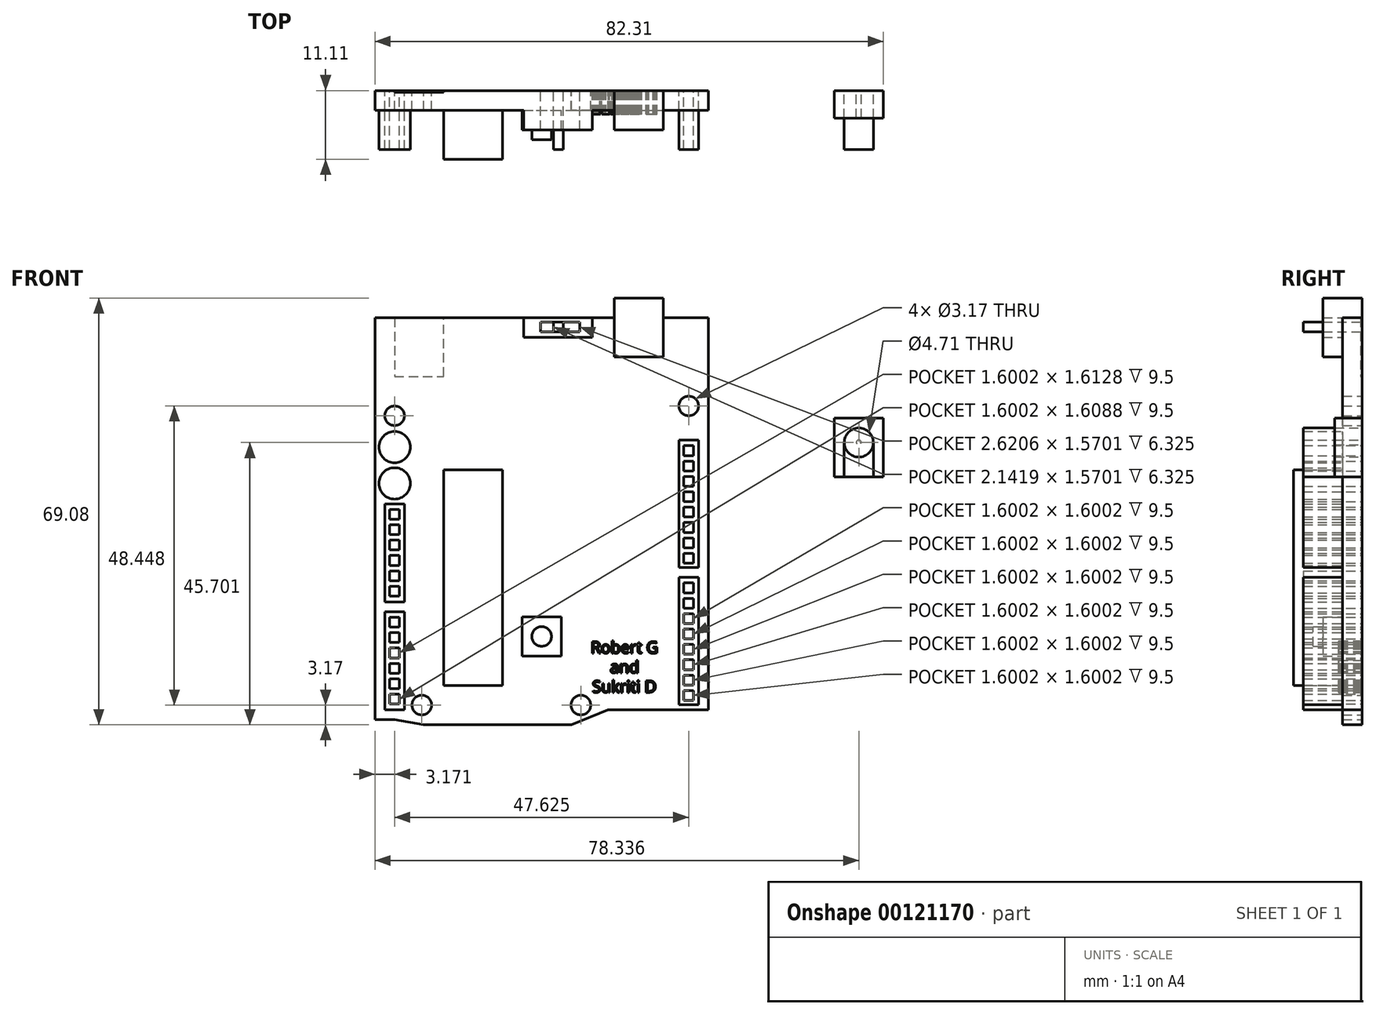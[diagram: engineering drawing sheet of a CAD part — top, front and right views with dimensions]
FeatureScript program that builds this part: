
annotation { "Feature Type Name" : "Feature", "Feature Type Description" : "" }
export const myFeature = defineFeature(function(context is Context, id is Id, definition is map)
    precondition{}
    {
        {
            var Q0;
            Q0=qCreatedBy(makeId("Front.planeOp"),FACE);
            var sketch = newSketch(context, id + "F0", { "sketchPlane" : qUnion([Q0])});
            skLineSegment(sketch, "E0.bottom", {"start": v(-35.3, 35.34) * mm, "end": v(18.68, 35.34) * mm});
            skLineSegment(sketch, "E0.top", {"start": v(-27.43, -30.57) * mm, "end": v(-3.44, -30.57) * mm});
            skLineSegment(sketch, "E0.left", {"start": v(-35.3, 35.34) * mm, "end": v(-35.3, -29.75) * mm});
            skLineSegment(sketch, "E0.right", {"start": v(18.68, 35.34) * mm, "end": v(18.68, -28.16) * mm});
            skLineSegment(sketch, "E1.bottom", {"start": v(-35.3, -29.75) * mm, "end": v(-32.12, -29.75) * mm});
            skPoint(sketch, "E2", {"position": v(-3.44, -30.57) * mm});
            skPoint(sketch, "E3.orphan", {"position": v(18.68, -30.57) * mm});
            skLineSegment(sketch, "E4", {"start": v(-32.12, -29.75) * mm, "end": v(-27.43, -30.57) * mm});
            skPoint(sketch, "E1.right.end.orphan", {"position": v(-35.19, -30.57) * mm});
            skLineSegment(sketch, "E5", {"start": v(-3.44, -30.57) * mm, "end": v(0.98, -28.76) * mm});
            skLineSegment(sketch, "E6", {"start": v(2.42, -28.16) * mm, "end": v(18.68, -28.16) * mm});
            skPoint(sketch, "E7.orphan", {"position": v(18.68, -30.95) * mm});
            skLineSegment(sketch, "E8", {"start": v(0.98, -28.76) * mm, "end": v(2.42, -28.16) * mm});
            skCircle(sketch, "E9", {"center": v(-27.72, -27.39) * mm, "radius": 1.59 * mm});
            skCircle(sketch, "E10", {"center": v(-1.96, -27.4) * mm, "radius": 1.59 * mm});
            skCircle(sketch, "E11", {"center": v(-32.12, 19.46) * mm, "radius": 1.59 * mm});
            skCircle(sketch, "E12", {"center": v(15.5, 21.05) * mm, "radius": 1.59 * mm});
            skLineSegment(sketch, "E13.bottom", {"start": v(11.14, 38.51) * mm, "end": v(11.4, 38.51) * mm});
            skLineSegment(sketch, "E13.top", {"start": v(3.47, 28.99) * mm, "end": v(11.4, 28.99) * mm});
            skLineSegment(sketch, "E14.bottom", {"start": v(13.92, -6.73) * mm, "end": v(17.1, -6.73) * mm});
            skLineSegment(sketch, "E14.top", {"start": v(13.92, -27.37) * mm, "end": v(17.1, -27.37) * mm});
            skLineSegment(sketch, "E14.left", {"start": v(13.92, -6.73) * mm, "end": v(13.92, -27.37) * mm});
            skLineSegment(sketch, "E14.right", {"start": v(17.1, -6.73) * mm, "end": v(17.1, -27.37) * mm});
            skLineSegment(sketch, "E15.bottom", {"start": v(13.92, 15.5) * mm, "end": v(17.1, 15.5) * mm});
            skLineSegment(sketch, "E15.top", {"start": v(13.92, -5.14) * mm, "end": v(17.1, -5.14) * mm});
            skLineSegment(sketch, "E15.left", {"start": v(13.92, 15.5) * mm, "end": v(13.92, -5.14) * mm});
            skLineSegment(sketch, "E15.right", {"start": v(17.1, 15.5) * mm, "end": v(17.1, -5.14) * mm});
            skLineSegment(sketch, "E16.bottom", {"start": v(-33.7, -12.29) * mm, "end": v(-30.53, -12.29) * mm});
            skLineSegment(sketch, "E16.top", {"start": v(-33.7, -28.16) * mm, "end": v(-30.53, -28.16) * mm});
            skLineSegment(sketch, "E16.left", {"start": v(-33.7, -12.29) * mm, "end": v(-33.7, -28.16) * mm});
            skLineSegment(sketch, "E16.right", {"start": v(-30.53, -12.29) * mm, "end": v(-30.53, -28.16) * mm});
            skLineSegment(sketch, "E17", {"start": v(-3.44, -30.57) * mm, "end": v(2.42, -28.16) * mm});
            skLineSegment(sketch, "E18.bottom", {"start": v(-33.7, 5.17) * mm, "end": v(-30.53, 5.17) * mm});
            skLineSegment(sketch, "E18.top", {"start": v(-33.7, -10.7) * mm, "end": v(-30.53, -10.7) * mm});
            skLineSegment(sketch, "E18.left", {"start": v(-33.7, 5.17) * mm, "end": v(-33.7, -10.7) * mm});
            skLineSegment(sketch, "E18.right", {"start": v(-30.53, 5.17) * mm, "end": v(-30.53, -10.7) * mm});
            skLineSegment(sketch, "E19.bottom", {"start": v(-24.18, -24.22) * mm, "end": v(-14.66, -24.22) * mm});
            skLineSegment(sketch, "E19.top", {"start": v(-24.18, 10.7) * mm, "end": v(-14.66, 10.7) * mm});
            skLineSegment(sketch, "E19.left", {"start": v(-24.18, -24.22) * mm, "end": v(-24.18, 10.7) * mm});
            skLineSegment(sketch, "E19.right", {"start": v(-14.66, -24.22) * mm, "end": v(-14.66, 10.7) * mm});
            skLineSegment(sketch, "E20.bottom", {"start": v(-11.48, -13.11) * mm, "end": v(-5.13, -13.11) * mm});
            skLineSegment(sketch, "E20.top", {"start": v(-11.48, -19.46) * mm, "end": v(-5.13, -19.46) * mm});
            skLineSegment(sketch, "E20.left", {"start": v(-11.48, -13.11) * mm, "end": v(-11.48, -19.46) * mm});
            skLineSegment(sketch, "E20.right", {"start": v(-5.13, -13.11) * mm, "end": v(-5.13, -19.46) * mm});
            skCircle(sketch, "E21", {"center": v(-8.3, -16.29) * mm, "radius": 1.59 * mm});
            skLineSegment(sketch, "E22.bottom", {"start": v(-11.2, 32.16) * mm, "end": v(-0.08, 32.16) * mm});
            skLineSegment(sketch, "E22.top", {"start": v(-11.2, 35.34) * mm, "end": v(-0.08, 35.34) * mm});
            skLineSegment(sketch, "E22.left", {"start": v(-11.2, 32.16) * mm, "end": v(-11.2, 35.34) * mm});
            skLineSegment(sketch, "E22.right", {"start": v(-0.08, 32.16) * mm, "end": v(-0.08, 35.34) * mm});
            skLineSegment(sketch, "E23.bottom", {"start": v(-8.5, 33.07) * mm, "end": v(-2.16, 33.07) * mm});
            skLineSegment(sketch, "E23.top", {"start": v(-8.5, 34.64) * mm, "end": v(-2.16, 34.64) * mm});
            skLineSegment(sketch, "E23.left", {"start": v(-8.5, 33.07) * mm, "end": v(-8.5, 34.64) * mm});
            skLineSegment(sketch, "E24", {"start": v(-2.16, 34.64) * mm, "end": v(-2.16, 33.07) * mm});
            skLineSegment(sketch, "E25", {"start": v(-4.78, 34.64) * mm, "end": v(-4.78, 33.07) * mm});
            skLineSegment(sketch, "E26", {"start": v(-6.37, 34.64) * mm, "end": v(-6.37, 33.07) * mm});
            skLineSegment(sketch, "E27", {"start": v(11.4, 36.51) * mm, "end": v(11.4, 35.34) * mm});
            skLineSegment(sketch, "E28.trimOffspring", {"start": v(3.47, 35.34) * mm, "end": v(3.47, 28.99) * mm});
            skLineSegment(sketch, "E29.trimOffspring", {"start": v(11.4, 35.34) * mm, "end": v(11.4, 28.99) * mm});
            skPoint(sketch, "E30.orphan", {"position": v(3.47, 38.51) * mm});
            skLineSegment(sketch, "E31", {"start": v(3.47, 35.34) * mm, "end": v(3.47, 36.51) * mm});
            skLineSegment(sketch, "E32", {"start": v(11.14, 38.51) * mm, "end": v(3.73, 38.51) * mm});
            skLineSegment(sketch, "E33", {"start": v(-32.12, 35.34) * mm, "end": v(-32.12, 25.81) * mm});
            skLineSegment(sketch, "E34", {"start": v(-32.12, 25.81) * mm, "end": v(-24.17, 25.81) * mm});
            skLineSegment(sketch, "E35", {"start": v(-24.17, 25.81) * mm, "end": v(-24.17, 35.34) * mm});
            skLineSegment(sketch, "E36.bottom", {"start": v(-32.9, 4.28) * mm, "end": v(-31.32, 4.28) * mm});
            skLineSegment(sketch, "E36.top", {"start": v(-32.9, 2.7) * mm, "end": v(-31.32, 2.7) * mm});
            skLineSegment(sketch, "E36.left", {"start": v(-32.9, 4.28) * mm, "end": v(-32.9, 2.7) * mm});
            skLineSegment(sketch, "E36.right", {"start": v(-31.32, 4.28) * mm, "end": v(-31.32, 2.7) * mm});
            skLineSegment(sketch, "E37.left", {"start": v(-32.9, 1.25) * mm, "end": v(-32.9, 1.22) * mm});
            skLineSegment(sketch, "E37.right", {"start": v(-31.53, 1.25) * mm, "end": v(-31.53, 1.22) * mm});
            skLineSegment(sketch, "E38.bottom", {"start": v(-32.9, 1.8) * mm, "end": v(-31.32, 1.8) * mm});
            skLineSegment(sketch, "E38.top", {"start": v(-32.9, 0.2) * mm, "end": v(-31.32, 0.2) * mm});
            skLineSegment(sketch, "E38.left", {"start": v(-32.9, 1.8) * mm, "end": v(-32.9, 0.2) * mm});
            skLineSegment(sketch, "E38.right", {"start": v(-31.32, 1.8) * mm, "end": v(-31.32, 0.2) * mm});
            skLineSegment(sketch, "E39.bottom", {"start": v(-32.9, -0.68) * mm, "end": v(-31.32, -0.68) * mm});
            skLineSegment(sketch, "E39.top", {"start": v(-32.9, -2.28) * mm, "end": v(-31.32, -2.28) * mm});
            skLineSegment(sketch, "E39.left", {"start": v(-32.9, -0.68) * mm, "end": v(-32.9, -2.28) * mm});
            skLineSegment(sketch, "E39.right", {"start": v(-31.32, -0.68) * mm, "end": v(-31.32, -2.28) * mm});
            skLineSegment(sketch, "E40.bottom", {"start": v(-32.9, -3.17) * mm, "end": v(-31.32, -3.17) * mm});
            skLineSegment(sketch, "E40.top", {"start": v(-32.9, -4.77) * mm, "end": v(-31.32, -4.77) * mm});
            skLineSegment(sketch, "E40.left", {"start": v(-32.9, -3.17) * mm, "end": v(-32.9, -4.77) * mm});
            skLineSegment(sketch, "E40.right", {"start": v(-31.32, -3.17) * mm, "end": v(-31.32, -4.77) * mm});
            skLineSegment(sketch, "E41.bottom", {"start": v(-32.9, -5.66) * mm, "end": v(-31.32, -5.66) * mm});
            skLineSegment(sketch, "E41.top", {"start": v(-32.9, -7.26) * mm, "end": v(-31.32, -7.26) * mm});
            skLineSegment(sketch, "E41.left", {"start": v(-32.9, -5.66) * mm, "end": v(-32.9, -7.26) * mm});
            skLineSegment(sketch, "E41.right", {"start": v(-31.32, -5.66) * mm, "end": v(-31.32, -7.26) * mm});
            skLineSegment(sketch, "E42.bottom", {"start": v(-32.9, -8.15) * mm, "end": v(-31.32, -8.15) * mm});
            skLineSegment(sketch, "E42.top", {"start": v(-32.9, -9.75) * mm, "end": v(-31.32, -9.75) * mm});
            skLineSegment(sketch, "E42.left", {"start": v(-32.9, -8.15) * mm, "end": v(-32.9, -9.75) * mm});
            skLineSegment(sketch, "E42.right", {"start": v(-31.32, -8.15) * mm, "end": v(-31.32, -9.75) * mm});
            skLineSegment(sketch, "E43.bottom", {"start": v(-32.92, -13.18) * mm, "end": v(-31.32, -13.18) * mm});
            skLineSegment(sketch, "E43.top", {"start": v(-32.92, -14.78) * mm, "end": v(-31.32, -14.78) * mm});
            skLineSegment(sketch, "E43.left", {"start": v(-32.92, -13.18) * mm, "end": v(-32.92, -14.78) * mm});
            skLineSegment(sketch, "E43.right", {"start": v(-31.32, -13.18) * mm, "end": v(-31.32, -14.78) * mm});
            skLineSegment(sketch, "E44.bottom", {"start": v(-32.92, -15.67) * mm, "end": v(-31.32, -15.67) * mm});
            skLineSegment(sketch, "E44.top", {"start": v(-32.92, -17.27) * mm, "end": v(-31.32, -17.27) * mm});
            skLineSegment(sketch, "E44.left", {"start": v(-32.92, -15.67) * mm, "end": v(-32.92, -17.27) * mm});
            skLineSegment(sketch, "E44.right", {"start": v(-31.32, -15.67) * mm, "end": v(-31.32, -17.27) * mm});
            skLineSegment(sketch, "E45.bottom", {"start": v(-32.92, -18.16) * mm, "end": v(-31.32, -18.16) * mm});
            skLineSegment(sketch, "E45.top", {"start": v(-32.92, -19.77) * mm, "end": v(-31.32, -19.77) * mm});
            skLineSegment(sketch, "E45.left", {"start": v(-32.92, -18.16) * mm, "end": v(-32.92, -19.77) * mm});
            skLineSegment(sketch, "E45.right", {"start": v(-31.32, -18.16) * mm, "end": v(-31.32, -19.77) * mm});
            skLineSegment(sketch, "E46.bottom", {"start": v(-32.92, -20.66) * mm, "end": v(-31.32, -20.66) * mm});
            skLineSegment(sketch, "E46.top", {"start": v(-32.92, -22.26) * mm, "end": v(-31.32, -22.26) * mm});
            skLineSegment(sketch, "E46.left", {"start": v(-32.92, -20.66) * mm, "end": v(-32.92, -22.26) * mm});
            skLineSegment(sketch, "E46.right", {"start": v(-31.32, -20.66) * mm, "end": v(-31.32, -22.26) * mm});
            skLineSegment(sketch, "E47.bottom", {"start": v(-32.92, -23.15) * mm, "end": v(-31.32, -23.15) * mm});
            skLineSegment(sketch, "E47.top", {"start": v(-32.92, -24.74) * mm, "end": v(-31.32, -24.74) * mm});
            skLineSegment(sketch, "E47.left", {"start": v(-32.92, -23.15) * mm, "end": v(-32.92, -24.74) * mm});
            skLineSegment(sketch, "E47.right", {"start": v(-31.32, -23.15) * mm, "end": v(-31.32, -24.74) * mm});
            skLineSegment(sketch, "E48.bottom", {"start": v(-32.92, -25.62) * mm, "end": v(-31.32, -25.62) * mm});
            skLineSegment(sketch, "E48.top", {"start": v(-32.92, -27.23) * mm, "end": v(-31.32, -27.23) * mm});
            skLineSegment(sketch, "E48.left", {"start": v(-32.92, -25.62) * mm, "end": v(-32.92, -27.23) * mm});
            skLineSegment(sketch, "E48.right", {"start": v(-31.32, -25.62) * mm, "end": v(-31.32, -27.23) * mm});
            skLineSegment(sketch, "E49.bottom", {"start": v(14.7, 14.6) * mm, "end": v(16.3, 14.6) * mm});
            skLineSegment(sketch, "E49.top", {"start": v(14.7, 13) * mm, "end": v(16.3, 13) * mm});
            skLineSegment(sketch, "E49.left", {"start": v(14.7, 14.6) * mm, "end": v(14.7, 13) * mm});
            skLineSegment(sketch, "E49.right", {"start": v(16.3, 14.6) * mm, "end": v(16.3, 13) * mm});
            skLineSegment(sketch, "E50.bottom", {"start": v(14.7, 12.12) * mm, "end": v(16.3, 12.12) * mm});
            skLineSegment(sketch, "E50.top", {"start": v(14.7, 10.52) * mm, "end": v(16.3, 10.52) * mm});
            skLineSegment(sketch, "E50.left", {"start": v(14.7, 12.12) * mm, "end": v(14.7, 10.52) * mm});
            skLineSegment(sketch, "E50.right", {"start": v(16.3, 12.12) * mm, "end": v(16.3, 10.52) * mm});
            skLineSegment(sketch, "E51.bottom", {"start": v(14.7, 9.63) * mm, "end": v(16.3, 9.63) * mm});
            skLineSegment(sketch, "E51.top", {"start": v(14.7, 8.03) * mm, "end": v(16.3, 8.03) * mm});
            skLineSegment(sketch, "E51.left", {"start": v(14.7, 9.63) * mm, "end": v(14.7, 8.03) * mm});
            skLineSegment(sketch, "E51.right", {"start": v(16.3, 9.63) * mm, "end": v(16.3, 8.03) * mm});
            skLineSegment(sketch, "E52.bottom", {"start": v(14.7, 7.14) * mm, "end": v(16.3, 7.14) * mm});
            skLineSegment(sketch, "E52.top", {"start": v(14.7, 5.54) * mm, "end": v(16.3, 5.54) * mm});
            skLineSegment(sketch, "E52.left", {"start": v(14.7, 7.14) * mm, "end": v(14.7, 5.54) * mm});
            skLineSegment(sketch, "E52.right", {"start": v(16.3, 7.14) * mm, "end": v(16.3, 5.54) * mm});
            skLineSegment(sketch, "E53.bottom", {"start": v(14.7, 4.65) * mm, "end": v(16.3, 4.65) * mm});
            skLineSegment(sketch, "E53.top", {"start": v(14.7, 3.05) * mm, "end": v(16.3, 3.05) * mm});
            skLineSegment(sketch, "E53.left", {"start": v(14.7, 4.65) * mm, "end": v(14.7, 3.05) * mm});
            skLineSegment(sketch, "E53.right", {"start": v(16.3, 4.65) * mm, "end": v(16.3, 3.05) * mm});
            skLineSegment(sketch, "E54.bottom", {"start": v(14.7, 2.16) * mm, "end": v(16.3, 2.16) * mm});
            skLineSegment(sketch, "E54.top", {"start": v(14.7, 0.56) * mm, "end": v(16.3, 0.56) * mm});
            skLineSegment(sketch, "E54.left", {"start": v(14.7, 2.16) * mm, "end": v(14.7, 0.56) * mm});
            skLineSegment(sketch, "E54.right", {"start": v(16.3, 2.16) * mm, "end": v(16.3, 0.56) * mm});
            skLineSegment(sketch, "E55.bottom", {"start": v(14.7, -0.33) * mm, "end": v(16.3, -0.33) * mm});
            skLineSegment(sketch, "E55.top", {"start": v(14.7, -1.92) * mm, "end": v(16.3, -1.92) * mm});
            skLineSegment(sketch, "E55.left", {"start": v(14.7, -0.33) * mm, "end": v(14.7, -1.92) * mm});
            skLineSegment(sketch, "E55.right", {"start": v(16.3, -0.33) * mm, "end": v(16.3, -1.92) * mm});
            skLineSegment(sketch, "E56.bottom", {"start": v(14.7, -2.8) * mm, "end": v(16.3, -2.8) * mm});
            skLineSegment(sketch, "E56.top", {"start": v(14.7, -4.4) * mm, "end": v(16.3, -4.4) * mm});
            skLineSegment(sketch, "E56.left", {"start": v(14.7, -2.8) * mm, "end": v(14.7, -4.4) * mm});
            skLineSegment(sketch, "E56.right", {"start": v(16.3, -2.8) * mm, "end": v(16.3, -4.4) * mm});
            skLineSegment(sketch, "E57.bottom", {"start": v(14.7, -7.62) * mm, "end": v(16.3, -7.62) * mm});
            skLineSegment(sketch, "E57.top", {"start": v(14.7, -9.22) * mm, "end": v(16.3, -9.22) * mm});
            skLineSegment(sketch, "E57.left", {"start": v(14.7, -7.62) * mm, "end": v(14.7, -9.22) * mm});
            skLineSegment(sketch, "E57.right", {"start": v(16.3, -7.62) * mm, "end": v(16.3, -9.22) * mm});
            skLineSegment(sketch, "E58.bottom", {"start": v(14.7, -10.1) * mm, "end": v(16.3, -10.1) * mm});
            skLineSegment(sketch, "E58.top", {"start": v(14.7, -11.7) * mm, "end": v(16.3, -11.7) * mm});
            skLineSegment(sketch, "E58.left", {"start": v(14.7, -10.1) * mm, "end": v(14.7, -11.7) * mm});
            skLineSegment(sketch, "E58.right", {"start": v(16.3, -10.1) * mm, "end": v(16.3, -11.7) * mm});
            skLineSegment(sketch, "E59.bottom", {"start": v(14.7, -12.6) * mm, "end": v(16.3, -12.6) * mm});
            skLineSegment(sketch, "E59.top", {"start": v(14.7, -14.2) * mm, "end": v(16.3, -14.2) * mm});
            skLineSegment(sketch, "E59.left", {"start": v(14.7, -12.6) * mm, "end": v(14.7, -14.2) * mm});
            skLineSegment(sketch, "E59.right", {"start": v(16.3, -12.6) * mm, "end": v(16.3, -14.2) * mm});
            skLineSegment(sketch, "E60.bottom", {"start": v(14.7, -15.09) * mm, "end": v(16.3, -15.09) * mm});
            skLineSegment(sketch, "E60.top", {"start": v(14.7, -16.69) * mm, "end": v(16.3, -16.69) * mm});
            skLineSegment(sketch, "E60.left", {"start": v(14.7, -15.09) * mm, "end": v(14.7, -16.69) * mm});
            skLineSegment(sketch, "E60.right", {"start": v(16.3, -15.09) * mm, "end": v(16.3, -16.69) * mm});
            skLineSegment(sketch, "E61.bottom", {"start": v(14.7, -17.58) * mm, "end": v(16.3, -17.58) * mm});
            skLineSegment(sketch, "E61.top", {"start": v(14.7, -19.18) * mm, "end": v(16.3, -19.18) * mm});
            skLineSegment(sketch, "E61.left", {"start": v(14.7, -17.58) * mm, "end": v(14.7, -19.18) * mm});
            skLineSegment(sketch, "E61.right", {"start": v(16.3, -17.58) * mm, "end": v(16.3, -19.18) * mm});
            skLineSegment(sketch, "E62.bottom", {"start": v(14.7, -20.07) * mm, "end": v(16.3, -20.07) * mm});
            skLineSegment(sketch, "E62.top", {"start": v(14.7, -21.67) * mm, "end": v(16.3, -21.67) * mm});
            skLineSegment(sketch, "E62.left", {"start": v(14.7, -20.07) * mm, "end": v(14.7, -21.67) * mm});
            skLineSegment(sketch, "E62.right", {"start": v(16.3, -20.07) * mm, "end": v(16.3, -21.67) * mm});
            skLineSegment(sketch, "E63.bottom", {"start": v(14.7, -22.56) * mm, "end": v(16.3, -22.56) * mm});
            skLineSegment(sketch, "E63.top", {"start": v(14.7, -24.16) * mm, "end": v(16.3, -24.16) * mm});
            skLineSegment(sketch, "E63.left", {"start": v(14.7, -22.56) * mm, "end": v(14.7, -24.16) * mm});
            skLineSegment(sketch, "E63.right", {"start": v(16.3, -22.56) * mm, "end": v(16.3, -24.16) * mm});
            skLineSegment(sketch, "E64.bottom", {"start": v(14.7, -25.04) * mm, "end": v(16.3, -25.04) * mm});
            skLineSegment(sketch, "E64.top", {"start": v(14.7, -26.64) * mm, "end": v(16.3, -26.64) * mm});
            skLineSegment(sketch, "E64.left", {"start": v(14.7, -25.04) * mm, "end": v(14.7, -26.64) * mm});
            skLineSegment(sketch, "E64.right", {"start": v(16.3, -25.04) * mm, "end": v(16.3, -26.64) * mm});
            skPoint(sketch, "E65.end.orphan", {"position": v(3.73, 37.04) * mm});
            skPoint(sketch, "E66.end.orphan", {"position": v(11.14, 37.04) * mm});
            skLineSegment(sketch, "E67", {"start": v(11.4, 36.51) * mm, "end": v(11.4, 38.51) * mm});
            skLineSegment(sketch, "E68", {"start": v(3.47, 36.51) * mm, "end": v(3.47, 38.51) * mm});
            skLineSegment(sketch, "E69", {"start": v(3.47, 38.51) * mm, "end": v(3.73, 38.51) * mm});
            skCircle(sketch, "E70", {"center": v(-32.12, 8.5) * mm, "radius": 2.54 * mm});
            skCircle(sketch, "E71", {"center": v(-32.12, 14.38) * mm, "radius": 2.54 * mm});
            skPoint(sketch, "E72.left.end.orphan", {"position": v(13.92, 17.84) * mm});
            skPoint(sketch, "E72.bottom.start.orphan", {"position": v(13.92, 16.26) * mm});
            skPoint(sketch, "E72.right.end.orphan", {"position": v(17.1, 17.84) * mm});
            skSolve(sketch);
        }
        {
            var Q0;
            Q0=qCreatedBy(makeId("Front.planeOp"),FACE);
            var sketch = newSketch(context, id + "F1", { "sketchPlane" : qUnion([Q0])});
            skLineSegment(sketch, "E73.bottom", {"start": v(39.08, 19.07) * mm, "end": v(47.02, 19.07) * mm});
            skLineSegment(sketch, "E73.top", {"start": v(39.08, 9.55) * mm, "end": v(47.02, 9.55) * mm});
            skLineSegment(sketch, "E73.left", {"start": v(39.08, 19.07) * mm, "end": v(39.08, 9.55) * mm});
            skLineSegment(sketch, "E73.right", {"start": v(47.02, 19.07) * mm, "end": v(47.02, 9.55) * mm});
            skLineSegment(sketch, "E74", {"start": v(43.05, 12.83) * mm, "end": v(43.05, 12.72) * mm});
            skLineSegment(sketch, "E75", {"start": v(43.05, 12.83) * mm, "end": v(43.05, 12.78) * mm});
            skPoint(sketch, "E76.orphan", {"position": v(43.05, 9.55) * mm});
            skPoint(sketch, "E77", {"position": v(43.05, 17.49) * mm});
            skPoint(sketch, "E78.orphan", {"position": v(43.05, 19.07) * mm});
            skArc(sketch, "E79", {"start": v(43, 12.78) * mm, "mid": v(43.05, 12.78) * mm, "end": v(43.1, 12.78) * mm});
            skCircle(sketch, "E80", {"center": v(43.05, 15.13) * mm, "radius": 0.8 * mm});
            skLineSegment(sketch, "E81", {"start": v(40.7, 15.13) * mm, "end": v(40.7, 9.55) * mm});
            skLineSegment(sketch, "E82", {"start": v(45.4, 15.13) * mm, "end": v(45.4, 9.55) * mm});
            skArc(sketch, "E83.trimOffspring", {"start": v(45.4, 15.13) * mm, "mid": v(43.05, 17.49) * mm, "end": v(40.7, 15.13) * mm});
            skCircle(sketch, "E84", {"center": v(43.05, 15.13) * mm, "radius": 0.4 * mm});
            skArc(sketch, "E85", {"start": v(40.7, 15.13) * mm, "mid": v(43.05, 12.78) * mm, "end": v(45.4, 15.13) * mm});
            skSolve(sketch);
        }
        {
            var Q0;
            {var subQ7=sQuery(id+"F0.wireOp",EDGE,"E0.left");Q0=makeQuery(id+"F0.imprint","IMPRINT",FACE,{"disambiguationData":[TD([[makeQuery(id+"F0.imprint","IMPRINT",EDGE,{"derivedFrom":subQ7}),1.0]])]});}
            var Q1;
            {var subQ0=sQuery(id+"F0.wireOp",EDGE,"E33");Q1=makeQuery(id+"F0.imprint","IMPRINT",FACE,{"disambiguationData":[TD([[makeQuery(id+"F0.imprint","IMPRINT",EDGE,{"derivedFrom":subQ0}),1.0]])]});}
            extrude(context, id + "F2", {"entities" : qUnion([Q0, Q1]), "depth" : 3.17 * mm});
        }
        {
            var Q0;
            Q0=makeQuery(id+"F0.imprint","IMPRINT",FACE,{"disambiguationData":[TD([[makeQuery(id+"F0.imprint","IMPRINT",EDGE,{"derivedFrom":sQuery(id+"F0.wireOp",EDGE,"E22.bottom")}),1.0]])]});
            extrude(context, id + "F3", {"entities" : qUnion([Q0]), "operationType" : NewBodyOperationType.ADD, "depth" : 6.35 * mm});
        }
        {
            var Q0;
            {var subQ0=sQuery(id+"F0.wireOp",EDGE,"E25");Q0=makeQuery(id+"F0.imprint","IMPRINT",FACE,{"disambiguationData":[TD([[makeQuery(id+"F0.imprint","IMPRINT",EDGE,{"derivedFrom":subQ0}),-1.0]])]});}
            extrude(context, id + "F4", {"entities" : qUnion([Q0]), "operationType" : NewBodyOperationType.ADD, "depth" : 9.52 * mm});
        }
        {
            var Q0;
            Q0=makeQuery(id+"F0.imprint","IMPRINT",FACE,{"disambiguationData":[TD([[makeQuery(id+"F0.imprint","IMPRINT",EDGE,{"derivedFrom":sQuery(id+"F0.wireOp",EDGE,"E14.bottom")}),-1.0]])]});
            var Q1;
            Q1=makeQuery(id+"F0.imprint","IMPRINT",FACE,{"disambiguationData":[TD([[makeQuery(id+"F0.imprint","IMPRINT",EDGE,{"derivedFrom":sQuery(id+"F0.wireOp",EDGE,"E15.bottom")}),-1.0]])]});
            var Q2;
            Q2=makeQuery(id+"F0.imprint","IMPRINT",FACE,{"disambiguationData":[TD([[makeQuery(id+"F0.imprint","IMPRINT",EDGE,{"derivedFrom":sQuery(id+"F0.wireOp",EDGE,"E18.bottom")}),-1.0]])]});
            var Q3;
            Q3=makeQuery(id+"F0.imprint","IMPRINT",FACE,{"disambiguationData":[TD([[makeQuery(id+"F0.imprint","IMPRINT",EDGE,{"derivedFrom":sQuery(id+"F0.wireOp",EDGE,"E16.bottom")}),-1.0]])]});
            extrude(context, id + "F5", {"entities" : qUnion([Q0, Q1, Q2, Q3]), "operationType" : NewBodyOperationType.ADD, "depth" : 9.52 * mm});
        }
        {
            var Q0;
            Q0=makeQuery(id+"F0.imprint","IMPRINT",FACE,{"disambiguationData":[TD([[makeQuery(id+"F0.imprint","IMPRINT",EDGE,{"derivedFrom":sQuery(id+"F0.wireOp",EDGE,"E19.bottom")}),1.0]])]});
            extrude(context, id + "F6", {"entities" : qUnion([Q0]), "operationType" : NewBodyOperationType.ADD, "depth" : 11.1 * mm});
        }
        {
            var Q0;
            {var subQ0=sQuery(id+"F0.wireOp",EDGE,"E27");Q0=makeQuery(id+"F0.imprint","IMPRINT",FACE,{"disambiguationData":[TD([[makeQuery(id+"F0.imprint","IMPRINT",EDGE,{"derivedFrom":subQ0}),-1.0]])]});}
            var Q1;
            Q1=makeQuery(id+"F0.imprint","IMPRINT",FACE,{"disambiguationData":[TD([[makeQuery(id+"F0.imprint","IMPRINT",EDGE,{"derivedFrom":sQuery(id+"F0.wireOp",EDGE,"E13.top")}),1.0]])]});
            extrude(context, id + "F7", {"entities" : qUnion([Q0, Q1]), "operationType" : NewBodyOperationType.ADD, "depth" : 6.35 * mm});
        }
        {
            var Q0;
            Q0=makeQuery(id+"F0.imprint","IMPRINT",FACE,{"disambiguationData":[TD([[makeQuery(id+"F0.imprint","IMPRINT",EDGE,{"derivedFrom":sQuery(id+"F0.wireOp",EDGE,"E20.bottom")}),-1.0]])]});
            extrude(context, id + "F8", {"entities" : qUnion([Q0]), "operationType" : NewBodyOperationType.ADD, "depth" : 6.35 * mm});
        }
        {
            var Q0;
            Q0=makeQuery(id+"F0.imprint","IMPRINT",FACE,{"disambiguationData":[TD([[makeQuery(id+"F0.imprint","IMPRINT",EDGE,{"derivedFrom":sQuery(id+"F0.wireOp",EDGE,"E21")}),1.0]])]});
            extrude(context, id + "F9", {"entities" : qUnion([Q0]), "operationType" : NewBodyOperationType.ADD, "depth" : 7.94 * mm});
        }
        {
            var Q0;
            Q0=qCreatedBy(makeId("Front.planeOp"),FACE);
            var sketch = newSketch(context, id + "F10", { "sketchPlane" : qUnion([Q0])});
            skText(sketch, "E86", { "text": "Robert G", "fontName": "OpenSans-Regular.ttf"});
            skText(sketch, "E87", { "text": "and", "fontName": "OpenSans-Regular.ttf"});
            skText(sketch, "E88", { "text": "Sukriti D", "fontName": "OpenSans-Regular.ttf"});
            skLineSegment(sketch, "E89", {"start": v(5.01, -19.27) * mm, "end": v(5.01, -20.54) * mm, "construction": true});
            skLineSegment(sketch, "E90", {"start": v(5.01, -22.45) * mm, "end": v(5.01, -23.72) * mm, "construction": true});
            const initialGuessF10  = {"E86": [-0.00037, -0.019, 1, 0, 0.0019], "E87": [0.00277, -0.02217, 1, 0, 0.0019], "E88": [-0.00012, -0.02534, 1, 0, 0.0019]};
            skSetInitialGuess(sketch, initialGuessF10);
            skSolve(sketch);
        }
        {
            var Q0;
            {var subQ0=sQuery(id+"F0.wireOp",EDGE,"E33");Q0=makeQuery(id+"F0.imprint","IMPRINT",FACE,{"disambiguationData":[TD([[makeQuery(id+"F0.imprint","IMPRINT",EDGE,{"derivedFrom":subQ0}),1.0]])]});}
            extrude(context, id + "F11", {"entities" : qUnion([Q0]), "depth" : 0.25 * mm});
        }
        {
            var Q0;
            Q0=qSketchRegion(id+"F10",true);
            extrude(context, id + "F12", {"entities" : qUnion([Q0]), "depth" : 3.8 * mm});
        }
        {
            var Q0;
            Q0=makeQuery(id+"F1.imprint","IMPRINT",FACE,{"disambiguationData":[TD([[makeQuery(id+"F1.imprint","IMPRINT",EDGE,{"derivedFrom":sQuery(id+"F1.wireOp",EDGE,"E73.bottom")}),-1.0]])]});
            var Q1;
            {var subQ2=sQuery(id+"F1.wireOp",EDGE,"E81");Q1=makeQuery(id+"F1.imprint","IMPRINT",FACE,{"disambiguationData":[TD([[makeQuery(id+"F1.imprint","IMPRINT",EDGE,{"derivedFrom":subQ2}),1.0]])]});}
            var Q2;
            Q2=makeQuery(id+"F1.imprint","IMPRINT",FACE,{"disambiguationData":[TD([[makeQuery(id+"F1.imprint","IMPRINT",EDGE,{"derivedFrom":sQuery(id+"F1.wireOp",EDGE,"E84")}),1.0]])]});
            extrude(context, id + "F13", {"entities" : qUnion([Q0, Q1, Q2]), "depth" : 4.44 * mm});
        }
        {
            var Q0;
            Q0=makeQuery(id+"F1.imprint","IMPRINT",FACE,{"disambiguationData":[TD([[makeQuery(id+"F1.imprint","IMPRINT",EDGE,{"derivedFrom":sQuery(id+"F1.wireOp",EDGE,"E80")}),-1.0]])]});
            var Q1;
            {var subQ2=sQuery(id+"F1.wireOp",EDGE,"E81");Q1=makeQuery(id+"F1.imprint","IMPRINT",FACE,{"disambiguationData":[TD([[makeQuery(id+"F1.imprint","IMPRINT",EDGE,{"derivedFrom":subQ2}),1.0]])]});}
            var Q2;
            Q2=makeQuery(id+"F1.imprint","IMPRINT",FACE,{"disambiguationData":[TD([[makeQuery(id+"F1.imprint","IMPRINT",EDGE,{"derivedFrom":sQuery(id+"F1.wireOp",EDGE,"E80")}),1.0]])]});
            var Q3;
            Q3=makeQuery(id+"F1.imprint","IMPRINT",FACE,{"disambiguationData":[TD([[makeQuery(id+"F1.imprint","IMPRINT",EDGE,{"derivedFrom":sQuery(id+"F1.wireOp",EDGE,"E84")}),1.0]])]});
            extrude(context, id + "F14", {"entities" : qUnion([Q0, Q1, Q2, Q3]), "depth" : 9.52 * mm});
        }
        {
            var Q0;
            Q0=makeQuery(id+"F0.imprint","IMPRINT",FACE,{"disambiguationData":[TD([[makeQuery(id+"F0.imprint","IMPRINT",EDGE,{"derivedFrom":sQuery(id+"F0.wireOp",EDGE,"E39.bottom")}),-1.0]])]});
            var Q1;
            Q1=makeQuery(id+"F0.imprint","IMPRINT",FACE,{"disambiguationData":[TD([[makeQuery(id+"F0.imprint","IMPRINT",EDGE,{"derivedFrom":sQuery(id+"F0.wireOp",EDGE,"E38.bottom")}),-1.0]])]});
            var Q2;
            Q2=makeQuery(id+"F0.imprint","IMPRINT",FACE,{"disambiguationData":[TD([[makeQuery(id+"F0.imprint","IMPRINT",EDGE,{"derivedFrom":sQuery(id+"F0.wireOp",EDGE,"E36.bottom")}),-1.0]])]});
            var Q3;
            Q3=makeQuery(id+"F0.imprint","IMPRINT",FACE,{"disambiguationData":[TD([[makeQuery(id+"F0.imprint","IMPRINT",EDGE,{"derivedFrom":sQuery(id+"F0.wireOp",EDGE,"E40.bottom")}),-1.0]])]});
            var Q4;
            Q4=makeQuery(id+"F0.imprint","IMPRINT",FACE,{"disambiguationData":[TD([[makeQuery(id+"F0.imprint","IMPRINT",EDGE,{"derivedFrom":sQuery(id+"F0.wireOp",EDGE,"E42.bottom")}),-1.0]])]});
            var Q5;
            Q5=makeQuery(id+"F0.imprint","IMPRINT",FACE,{"disambiguationData":[TD([[makeQuery(id+"F0.imprint","IMPRINT",EDGE,{"derivedFrom":sQuery(id+"F0.wireOp",EDGE,"E41.bottom")}),-1.0]])]});
            extrude(context, id + "F15", {"entities" : qUnion([Q0, Q1, Q2, Q3, Q4, Q5]), "operationType" : NewBodyOperationType.ADD, "depth" : 0.03 * mm});
        }
        {
            var Q0;
            Q0=makeQuery(id+"F0.imprint","IMPRINT",FACE,{"disambiguationData":[TD([[makeQuery(id+"F0.imprint","IMPRINT",EDGE,{"derivedFrom":sQuery(id+"F0.wireOp",EDGE,"E43.bottom")}),-1.0]])]});
            var Q1;
            Q1=makeQuery(id+"F0.imprint","IMPRINT",FACE,{"disambiguationData":[TD([[makeQuery(id+"F0.imprint","IMPRINT",EDGE,{"derivedFrom":sQuery(id+"F0.wireOp",EDGE,"E44.bottom")}),-1.0]])]});
            var Q2;
            Q2=makeQuery(id+"F0.imprint","IMPRINT",FACE,{"disambiguationData":[TD([[makeQuery(id+"F0.imprint","IMPRINT",EDGE,{"derivedFrom":sQuery(id+"F0.wireOp",EDGE,"E45.bottom")}),-1.0]])]});
            var Q3;
            Q3=makeQuery(id+"F0.imprint","IMPRINT",FACE,{"disambiguationData":[TD([[makeQuery(id+"F0.imprint","IMPRINT",EDGE,{"derivedFrom":sQuery(id+"F0.wireOp",EDGE,"E46.bottom")}),-1.0]])]});
            var Q4;
            Q4=makeQuery(id+"F0.imprint","IMPRINT",FACE,{"disambiguationData":[TD([[makeQuery(id+"F0.imprint","IMPRINT",EDGE,{"derivedFrom":sQuery(id+"F0.wireOp",EDGE,"E47.bottom")}),-1.0]])]});
            var Q5;
            Q5=makeQuery(id+"F0.imprint","IMPRINT",FACE,{"disambiguationData":[TD([[makeQuery(id+"F0.imprint","IMPRINT",EDGE,{"derivedFrom":sQuery(id+"F0.wireOp",EDGE,"E48.bottom")}),-1.0]])]});
            extrude(context, id + "F16", {"entities" : qUnion([Q0, Q1, Q2, Q3, Q4, Q5]), "operationType" : NewBodyOperationType.ADD, "depth" : 0.03 * mm});
        }
        {
            var Q0;
            Q0=makeQuery(id+"F0.imprint","IMPRINT",FACE,{"disambiguationData":[TD([[makeQuery(id+"F0.imprint","IMPRINT",EDGE,{"derivedFrom":sQuery(id+"F0.wireOp",EDGE,"E49.bottom")}),-1.0]])]});
            var Q1;
            Q1=makeQuery(id+"F0.imprint","IMPRINT",FACE,{"disambiguationData":[TD([[makeQuery(id+"F0.imprint","IMPRINT",EDGE,{"derivedFrom":sQuery(id+"F0.wireOp",EDGE,"E55.bottom")}),-1.0]])]});
            var Q2;
            Q2=makeQuery(id+"F0.imprint","IMPRINT",FACE,{"disambiguationData":[TD([[makeQuery(id+"F0.imprint","IMPRINT",EDGE,{"derivedFrom":sQuery(id+"F0.wireOp",EDGE,"E54.bottom")}),-1.0]])]});
            var Q3;
            Q3=makeQuery(id+"F0.imprint","IMPRINT",FACE,{"disambiguationData":[TD([[makeQuery(id+"F0.imprint","IMPRINT",EDGE,{"derivedFrom":sQuery(id+"F0.wireOp",EDGE,"E53.bottom")}),-1.0]])]});
            var Q4;
            Q4=makeQuery(id+"F0.imprint","IMPRINT",FACE,{"disambiguationData":[TD([[makeQuery(id+"F0.imprint","IMPRINT",EDGE,{"derivedFrom":sQuery(id+"F0.wireOp",EDGE,"E52.bottom")}),-1.0]])]});
            var Q5;
            Q5=makeQuery(id+"F0.imprint","IMPRINT",FACE,{"disambiguationData":[TD([[makeQuery(id+"F0.imprint","IMPRINT",EDGE,{"derivedFrom":sQuery(id+"F0.wireOp",EDGE,"E51.bottom")}),-1.0]])]});
            var Q6;
            Q6=makeQuery(id+"F0.imprint","IMPRINT",FACE,{"disambiguationData":[TD([[makeQuery(id+"F0.imprint","IMPRINT",EDGE,{"derivedFrom":sQuery(id+"F0.wireOp",EDGE,"E50.bottom")}),-1.0]])]});
            var Q7;
            Q7=makeQuery(id+"F0.imprint","IMPRINT",FACE,{"disambiguationData":[TD([[makeQuery(id+"F0.imprint","IMPRINT",EDGE,{"derivedFrom":sQuery(id+"F0.wireOp",EDGE,"E56.bottom")}),-1.0]])]});
            extrude(context, id + "F17", {"entities" : qUnion([Q0, Q1, Q2, Q3, Q4, Q5, Q6, Q7]), "operationType" : NewBodyOperationType.ADD, "depth" : 0.03 * mm});
        }
        {
            var Q0;
            {var subQ0=sQuery(id+"F0.wireOp",EDGE,"E24");Q0=makeQuery(id+"F0.imprint","IMPRINT",FACE,{"disambiguationData":[TD([[makeQuery(id+"F0.imprint","IMPRINT",EDGE,{"derivedFrom":subQ0}),-1.0]])]});}
            var Q1;
            {var subQ0=sQuery(id+"F0.wireOp",EDGE,"E23.left");Q1=makeQuery(id+"F0.imprint","IMPRINT",FACE,{"disambiguationData":[TD([[makeQuery(id+"F0.imprint","IMPRINT",EDGE,{"derivedFrom":subQ0}),-1.0]])]});}
            extrude(context, id + "F18", {"entities" : qUnion([Q0, Q1]), "operationType" : NewBodyOperationType.ADD, "depth" : 0.03 * mm});
        }
        {
            var Q0;
            Q0=makeQuery(id+"F0.imprint","IMPRINT",FACE,{"disambiguationData":[TD([[makeQuery(id+"F0.imprint","IMPRINT",EDGE,{"derivedFrom":sQuery(id+"F0.wireOp",EDGE,"E59.bottom")}),-1.0]])]});
            var Q1;
            Q1=makeQuery(id+"F0.imprint","IMPRINT",FACE,{"disambiguationData":[TD([[makeQuery(id+"F0.imprint","IMPRINT",EDGE,{"derivedFrom":sQuery(id+"F0.wireOp",EDGE,"E61.bottom")}),-1.0]])]});
            var Q2;
            Q2=makeQuery(id+"F0.imprint","IMPRINT",FACE,{"disambiguationData":[TD([[makeQuery(id+"F0.imprint","IMPRINT",EDGE,{"derivedFrom":sQuery(id+"F0.wireOp",EDGE,"E60.bottom")}),-1.0]])]});
            var Q3;
            Q3=makeQuery(id+"F0.imprint","IMPRINT",FACE,{"disambiguationData":[TD([[makeQuery(id+"F0.imprint","IMPRINT",EDGE,{"derivedFrom":sQuery(id+"F0.wireOp",EDGE,"E62.bottom")}),-1.0]])]});
            var Q4;
            Q4=makeQuery(id+"F0.imprint","IMPRINT",FACE,{"disambiguationData":[TD([[makeQuery(id+"F0.imprint","IMPRINT",EDGE,{"derivedFrom":sQuery(id+"F0.wireOp",EDGE,"E63.bottom")}),-1.0]])]});
            var Q5;
            Q5=makeQuery(id+"F0.imprint","IMPRINT",FACE,{"disambiguationData":[TD([[makeQuery(id+"F0.imprint","IMPRINT",EDGE,{"derivedFrom":sQuery(id+"F0.wireOp",EDGE,"E64.bottom")}),-1.0]])]});
            var Q6;
            Q6=makeQuery(id+"F0.imprint","IMPRINT",FACE,{"disambiguationData":[TD([[makeQuery(id+"F0.imprint","IMPRINT",EDGE,{"derivedFrom":sQuery(id+"F0.wireOp",EDGE,"E58.bottom")}),-1.0]])]});
            var Q7;
            Q7=makeQuery(id+"F0.imprint","IMPRINT",FACE,{"disambiguationData":[TD([[makeQuery(id+"F0.imprint","IMPRINT",EDGE,{"derivedFrom":sQuery(id+"F0.wireOp",EDGE,"E57.bottom")}),-1.0]])]});
            extrude(context, id + "F19", {"entities" : qUnion([Q0, Q1, Q2, Q3, Q4, Q5, Q6, Q7]), "operationType" : NewBodyOperationType.ADD, "depth" : 0.03 * mm});
        }
        {
            var Q0;
            Q0=makeQuery(id+"F0.imprint","IMPRINT",FACE,{"disambiguationData":[TD([[makeQuery(id+"F0.imprint","IMPRINT",EDGE,{"derivedFrom":sQuery(id+"F0.wireOp",EDGE,"E71")}),1.0]])]});
            var Q1;
            Q1=makeQuery(id+"F0.imprint","IMPRINT",FACE,{"disambiguationData":[TD([[makeQuery(id+"F0.imprint","IMPRINT",EDGE,{"derivedFrom":sQuery(id+"F0.wireOp",EDGE,"E70")}),1.0]])]});
            extrude(context, id + "F20", {"entities" : qUnion([Q0, Q1]), "operationType" : NewBodyOperationType.ADD, "depth" : 9.52 * mm});
        }
    });
